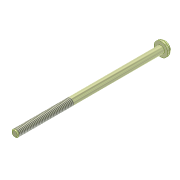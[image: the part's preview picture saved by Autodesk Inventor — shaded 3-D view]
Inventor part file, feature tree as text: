
AUTODESK INVENTOR PART (.ipt)
format: ipt  version: unknown  size: 186,880 bytes
history: native  units: mm
features: imported_body x1, thread x1
ambient origin geometry x8: Origin, YZ Plane, XZ Plane, XY Plane, X Axis, Y Axis, Z Axis, Center Point
bodies: Solid1 (feature_tree)
feature tree (2):
  imported_body  "Base1"
  thread  "Thread1"  [1 undecoded]
note: 1 required parameter value undecoded (feature->parameter linkage not recoverable at this tier; creation-order binding heuristic only, values carry confidence <= 0.55)
